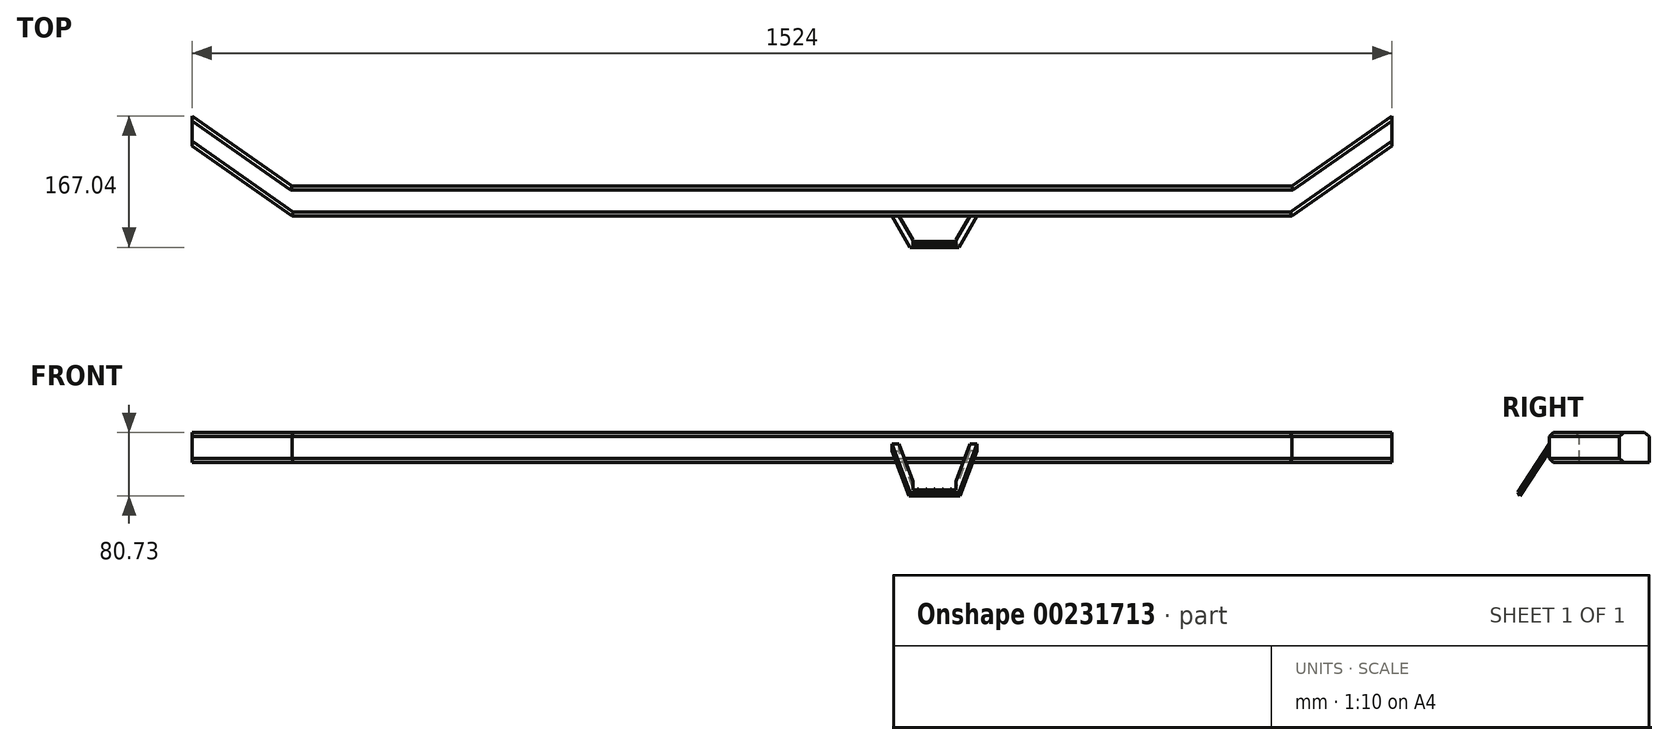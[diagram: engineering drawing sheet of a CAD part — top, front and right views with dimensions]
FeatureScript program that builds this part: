
annotation { "Feature Type Name" : "Feature", "Feature Type Description" : "" }
export const myFeature = defineFeature(function(context is Context, id is Id, definition is map)
    precondition{}
    {
        {
            var Q0;
            Q0=qCreatedBy(makeId("Top.planeOp"),FACE);
            var sketch = newSketch(context, id + "F0", { "sketchPlane" : qUnion([Q0])});
            skLineSegment(sketch, "E0", {"start": v(0, 0) * mm, "end": v(0, 180.16) * mm, "construction": true});
            skLineSegment(sketch, "E1", {"start": v(0, 0) * mm, "end": v(635, 0) * mm});
            skLineSegment(sketch, "E2", {"start": v(635, 0) * mm, "end": v(762, 88.9) * mm});
            skLineSegment(sketch, "E3.MirrorCS", {"start": v(0, 0) * mm, "end": v(-635, 0) * mm});
            skLineSegment(sketch, "E4.MirrorCS", {"start": v(-635, 0) * mm, "end": v(-762, 88.9) * mm});
            skSolve(sketch);
        }
        {
            var Q0;
            Q0=qCreatedBy(makeId("Right.planeOp"),FACE);
            var Q1;
            Q1=sQuery(id+"F0.wireOp",VERTEX,"E2.start");
            cPlane(context, id + "F1", {"entities" : qUnion([Q0, Q1]), "cplaneType" : CPlaneType.PLANE_POINT, "offset" : 25.4 * mm, "width" : 152.4 * mm, "height" : 152.4 * mm});
        }
        {
            var Q0;
            Q0=qCreatedBy(id+"F1.planeOp",FACE);
            var sketch = newSketch(context, id + "F2", { "sketchPlane" : qUnion([Q0])});
            skLineSegment(sketch, "E5.bottom", {"start": v(19.05, -19.05) * mm, "end": v(-19.05, -19.05) * mm});
            skLineSegment(sketch, "E5.top", {"start": v(19.05, 19.05) * mm, "end": v(-19.05, 19.05) * mm});
            skLineSegment(sketch, "E5.left", {"start": v(19.05, -19.05) * mm, "end": v(19.05, 19.05) * mm});
            skLineSegment(sketch, "E5.right", {"start": v(-19.05, -19.05) * mm, "end": v(-19.05, 19.05) * mm});
            skPoint(sketch, "E5.middle", {"position": v(0, 0) * mm});
            skSolve(sketch);
        }
        {
            var Q0;
            Q0=makeQuery(id+"F2.imprint","IMPRINT",FACE,{"disambiguationData":[TD([[makeQuery(id+"F2.imprint","IMPRINT",EDGE,{"derivedFrom":sQuery(id+"F2.wireOp",EDGE,"E5.bottom")}),-1.0]])]});
            var Q1;
            Q1=sQuery(id+"F0.wireOp",EDGE,"E2");
            sweep(context, id + "F3", {"profiles" : qUnion([Q0]), "path" : qUnion([Q1]), "keepProfileOrientation" : true});
        }
        {
            var Q0;
            Q0=makeQuery(id+"F2.imprint","IMPRINT",FACE,{"disambiguationData":[TD([[makeQuery(id+"F2.imprint","IMPRINT",EDGE,{"derivedFrom":sQuery(id+"F2.wireOp",EDGE,"E5.bottom")}),-1.0]])]});
            var Q1;
            Q1=sQuery(id+"F0.wireOp",EDGE,"E1");
            sweep(context, id + "F4", {"operationType" : NewBodyOperationType.ADD, "profiles" : qUnion([Q0]), "path" : qUnion([Q1])});
        }
        {
            var Q0;
            Q0=makeQuery(id+"F3.opSweep","SWEPT_BODY",BODY,{"disambiguationData":[OSD([sQuery(id+"F0.wireOp",EDGE,"E2"),sQuery(id+"F2.wireOp",EDGE,"E5.bottom"),sQuery(id+"F2.wireOp",EDGE,"E5.top"),sQuery(id+"F2.wireOp",EDGE,"E5.left"),sQuery(id+"F2.wireOp",EDGE,"E5.right")])]});
            var Q1;
            Q1=qCreatedBy(makeId("Right.planeOp"),FACE);
            mirror(context, id + "F5", {"operationType" : NewBodyOperationType.ADD, "entities" : qUnion([Q0]), "mirrorPlane" : qUnion([Q1])});
        }
        {
            var Q0;
            {var subQ0=makeQuery(id+"F4.opSweep","SWEPT_EDGE",EDGE,{"disambiguationData":[OSD([sQuery(id+"F0.wireOp",EDGE,"E1"),sQuery(id+"F2.wireOp",EDGE,"E5.top"),sQuery(id+"F2.wireOp",EDGE,"E5.right")])]});Q0=makeQuery(id+"F5.boolean.opBoolean","MERGE",EDGE,{"derivedFrom":[subQ0,makeQuery(id+"F5.opPattern","COPY",EDGE,{"derivedFrom":subQ0,"instanceName":"1"})]});}
            var Q1;
            Q1=makeQuery(id+"F5.opPattern","COPY",EDGE,{"derivedFrom":makeQuery(id+"F3.opSweep","SWEPT_EDGE",EDGE,{"disambiguationData":[OSD([sQuery(id+"F0.wireOp",EDGE,"E2"),sQuery(id+"F2.wireOp",EDGE,"E5.top"),sQuery(id+"F2.wireOp",EDGE,"E5.right")])]}),"instanceName":"1"});
            var Q2;
            Q2=makeQuery(id+"F5.opPattern","COPY",EDGE,{"derivedFrom":makeQuery(id+"F3.opSweep","SWEPT_EDGE",EDGE,{"disambiguationData":[OSD([sQuery(id+"F0.wireOp",EDGE,"E2"),sQuery(id+"F2.wireOp",EDGE,"E5.top"),sQuery(id+"F2.wireOp",EDGE,"E5.left")])]}),"instanceName":"1"});
            var Q3;
            {var subQ0=makeQuery(id+"F4.opSweep","SWEPT_EDGE",EDGE,{"disambiguationData":[OSD([sQuery(id+"F0.wireOp",EDGE,"E1"),sQuery(id+"F2.wireOp",EDGE,"E5.top"),sQuery(id+"F2.wireOp",EDGE,"E5.left")])]});Q3=makeQuery(id+"F5.boolean.opBoolean","MERGE",EDGE,{"derivedFrom":[subQ0,makeQuery(id+"F5.opPattern","COPY",EDGE,{"derivedFrom":subQ0,"instanceName":"1"})]});}
            var Q4;
            Q4=makeQuery(id+"F5.opPattern","COPY",EDGE,{"derivedFrom":makeQuery(id+"F3.opSweep","SWEPT_EDGE",EDGE,{"disambiguationData":[OSD([sQuery(id+"F0.wireOp",EDGE,"E2"),sQuery(id+"F2.wireOp",EDGE,"E5.bottom"),sQuery(id+"F2.wireOp",EDGE,"E5.right")])]}),"instanceName":"1"});
            var Q5;
            {var subQ0=makeQuery(id+"F4.opSweep","SWEPT_EDGE",EDGE,{"disambiguationData":[OSD([sQuery(id+"F0.wireOp",EDGE,"E1"),sQuery(id+"F2.wireOp",EDGE,"E5.bottom"),sQuery(id+"F2.wireOp",EDGE,"E5.right")])]});Q5=makeQuery(id+"F5.boolean.opBoolean","MERGE",EDGE,{"derivedFrom":[subQ0,makeQuery(id+"F5.opPattern","COPY",EDGE,{"derivedFrom":subQ0,"instanceName":"1"})]});}
            var Q6;
            Q6=makeQuery(id+"F3.opSweep","SWEPT_EDGE",EDGE,{"disambiguationData":[OSD([sQuery(id+"F0.wireOp",EDGE,"E2"),sQuery(id+"F2.wireOp",EDGE,"E5.top"),sQuery(id+"F2.wireOp",EDGE,"E5.right")])]});
            var Q7;
            Q7=makeQuery(id+"F3.opSweep","SWEPT_EDGE",EDGE,{"disambiguationData":[OSD([sQuery(id+"F0.wireOp",EDGE,"E2"),sQuery(id+"F2.wireOp",EDGE,"E5.top"),sQuery(id+"F2.wireOp",EDGE,"E5.left")])]});
            var Q8;
            Q8=makeQuery(id+"F3.opSweep","SWEPT_EDGE",EDGE,{"disambiguationData":[OSD([sQuery(id+"F0.wireOp",EDGE,"E2"),sQuery(id+"F2.wireOp",EDGE,"E5.bottom"),sQuery(id+"F2.wireOp",EDGE,"E5.right")])]});
            chamfer(context, id + "F6", {"entities" : qUnion([Q0, Q1, Q2, Q3, Q4, Q5, Q6, Q7, Q8]), "width" : 5.08 * mm, "tangentPropagation" : true});
        }
        {
            var Q0;
            Q0=makeQuery(id+"F3.opSweep","CAP_EDGE",EDGE,{"disambiguationData":[OSD([sQuery(id+"F0.wireOp",VERTEX,"E2.end"),sQuery(id+"F2.wireOp",EDGE,"E5.left")])],"isStart":false});
            cPlane(context, id + "F7", {"entities" : qUnion([Q0]), "cplaneType" : CPlaneType.LINE_ANGLE, "offset" : 25.4 * mm, "angle" : 30 * degree, "width" : 152.4 * mm, "height" : 152.4 * mm});
        }
        {
            var Q0;
            Q0=qCreatedBy(id+"F7.planeOp",FACE);
            cPlane(context, id + "F8", {"entities" : qUnion([Q0]), "cplaneType" : CPlaneType.OFFSET, "offset" : 609.6 * mm, "oppositeDirection" : true, "width" : 152.4 * mm, "height" : 152.4 * mm});
        }
        {
            var Q0;
            Q0=qCreatedBy(id+"F8.planeOp",FACE);
            var sketch = newSketch(context, id + "F9", { "sketchPlane" : qUnion([Q0])});
            skLineSegment(sketch, "E6", {"start": v(-82.2, 0) * mm, "end": v(-124.13, -55.87) * mm});
            skSolve(sketch);
        }
        {
            var Q0;
            {var subQ0=makeQuery(id+"F4.opSweep","SWEPT_FACE",FACE,{"disambiguationData":[OSD([sQuery(id+"F0.wireOp",EDGE,"E1"),sQuery(id+"F2.wireOp",EDGE,"E5.right")])]});Q0=makeQuery(id+"F5.boolean.opBoolean","MERGE",FACE,{"derivedFrom":[subQ0,makeQuery(id+"F5.opPattern","COPY",FACE,{"derivedFrom":subQ0,"instanceName":"1"})]});}
            var Q1;
            Q1=sQuery(id+"F9.wireOp",VERTEX,"E6.end");
            cPlane(context, id + "F10", {"entities" : qUnion([Q0, Q1]), "cplaneType" : CPlaneType.PLANE_POINT, "offset" : 25.4 * mm, "width" : 152.4 * mm, "height" : 152.4 * mm});
        }
        {
            var Q0;
            Q0=qCreatedBy(id+"F10.planeOp",FACE);
            var sketch = newSketch(context, id + "F11", { "sketchPlane" : qUnion([Q0])});
            skLineSegment(sketch, "E7", {"start": v(152.38, -55.87) * mm, "end": v(209.53, -55.87) * mm});
            skLineSegment(sketch, "E8", {"start": v(180.95, -55.87) * mm, "end": v(180.95, -95.2) * mm, "construction": true});
            skPoint(sketch, "E8.endSnap0", {"position": v(180.95, -55.87) * mm});
            skSolve(sketch);
        }
        {
            var Q0;
            Q0=makeQuery(id+"F3.opSweep","CAP_EDGE",EDGE,{"disambiguationData":[OSD([sQuery(id+"F0.wireOp",VERTEX,"E2.end"),sQuery(id+"F2.wireOp",EDGE,"E5.left")])],"isStart":false});
            cPlane(context, id + "F12", {"entities" : qUnion([Q0]), "cplaneType" : CPlaneType.LINE_ANGLE, "offset" : 25.4 * mm, "angle" : 330 * degree, "width" : 152.4 * mm, "height" : 152.4 * mm});
        }
        {
            var Q0;
            Q0=qCreatedBy(id+"F12.planeOp",FACE);
            var Q1;
            Q1=sQuery(id+"F11.wireOp",VERTEX,"E7.end");
            cPlane(context, id + "F13", {"entities" : qUnion([Q0, Q1]), "cplaneType" : CPlaneType.PLANE_POINT, "offset" : 25.4 * mm, "width" : 152.4 * mm, "height" : 152.4 * mm});
        }
        {
            var Q0;
            Q0=qCreatedBy(id+"F13.planeOp",FACE);
            var sketch = newSketch(context, id + "F14", { "sketchPlane" : qUnion([Q0])});
            skLineSegment(sketch, "E9", {"start": v(98.75, 0) * mm, "end": v(56.83, -55.87) * mm});
            skSolve(sketch);
        }
        {
            var Q0;
            {var subQ0=makeQuery(id+"F4.opSweep","SWEPT_FACE",FACE,{"disambiguationData":[OSD([sQuery(id+"F0.wireOp",EDGE,"E1"),sQuery(id+"F2.wireOp",EDGE,"E5.right")])]});Q0=makeQuery(id+"F5.boolean.opBoolean","MERGE",FACE,{"derivedFrom":[subQ0,makeQuery(id+"F5.opPattern","COPY",FACE,{"derivedFrom":subQ0,"instanceName":"1"})]});}
            var sketch = newSketch(context, id + "F15", { "sketchPlane" : qUnion([Q0])});
            skLineSegment(sketch, "E10.bottom", {"start": v(234.93, -4.44) * mm, "end": v(226.04, -4.44) * mm});
            skLineSegment(sketch, "E10.top", {"start": v(234.93, 4.45) * mm, "end": v(226.04, 4.44) * mm});
            skLineSegment(sketch, "E10.left", {"start": v(234.93, -4.44) * mm, "end": v(234.93, 4.45) * mm});
            skLineSegment(sketch, "E10.right", {"start": v(226.04, -4.44) * mm, "end": v(226.04, 4.44) * mm});
            skPoint(sketch, "E10.middle", {"position": v(230.49, 0) * mm});
            skSolve(sketch);
        }
        {
            var Q0;
            Q0=qCreatedBy(id+"F8.planeOp",FACE);
            var sketch = newSketch(context, id + "F16", { "sketchPlane" : qUnion([Q0])});
            skLineSegment(sketch, "E11", {"start": v(-82.2, 0) * mm, "end": v(-76.1, 8.13) * mm});
            skSolve(sketch);
        }
        {
            var Q0;
            Q0=makeQuery(id+"F15.imprint","IMPRINT",FACE,{"disambiguationData":[TD([[makeQuery(id+"F15.imprint","IMPRINT",EDGE,{"derivedFrom":sQuery(id+"F15.wireOp",EDGE,"E10.bottom")}),-1.0]])]});
            var Q1;
            Q1=sQuery(id+"F14.wireOp",EDGE,"E9");
            var Q2;
            Q2=sQuery(id+"F11.wireOp",EDGE,"E7");
            var Q3;
            Q3=sQuery(id+"F9.wireOp",EDGE,"E6");
            var Q4;
            Q4=sQuery(id+"F16.wireOp",EDGE,"E11");
            sweep(context, id + "F17", {"operationType" : NewBodyOperationType.ADD, "profiles" : qUnion([Q0]), "path" : qUnion([Q1, Q2, Q3, Q4])});
        }
        {
            var Q0;
            {var subQ0=makeQuery(id+"F4.opSweep","SWEPT_FACE",FACE,{"disambiguationData":[OSD([sQuery(id+"F0.wireOp",EDGE,"E1"),sQuery(id+"F2.wireOp",EDGE,"E5.right")])]});Q0=makeQuery(id+"F5.boolean.opBoolean","MERGE",FACE,{"derivedFrom":[subQ0,makeQuery(id+"F5.opPattern","COPY",FACE,{"derivedFrom":subQ0,"instanceName":"1"})]});}
            var Q1;
            Q1=makeQuery(id+"F17.opSweep","MID_CAP_VERTEX",VERTEX,{"disambiguationData":[OSD([sQuery(id+"F11.wireOp",EDGE,"E7"),sQuery(id+"F15.wireOp",EDGE,"E10.top"),sQuery(id+"F15.wireOp",EDGE,"E10.left")])],"capPos":2.0});
            cPlane(context, id + "F18", {"entities" : qUnion([Q0, Q1]), "cplaneType" : CPlaneType.PLANE_POINT, "offset" : 25.4 * mm, "width" : 152.4 * mm, "height" : 152.4 * mm});
        }
        {
            var Q0;
            Q0=qCreatedBy(id+"F18.planeOp",FACE);
            var sketch = newSketch(context, id + "F19", { "sketchPlane" : qUnion([Q0])});
            skLineSegment(sketch, "E12", {"start": v(180.95, -50.06) * mm, "end": v(180.95, -63.1) * mm, "construction": true});
            skLineSegment(sketch, "E13", {"start": v(153.65, -41.06) * mm, "end": v(180.95, -41.06) * mm});
            skLineSegment(sketch, "E14", {"start": v(153.65, -41.06) * mm, "end": v(153.65, -53.76) * mm});
            skLineSegment(sketch, "E15", {"start": v(153.65, -53.76) * mm, "end": v(180.95, -53.76) * mm});
            skLineSegment(sketch, "E16.MirrorCS", {"start": v(208.26, -53.76) * mm, "end": v(180.95, -53.76) * mm});
            skLineSegment(sketch, "E17.MirrorCS", {"start": v(208.26, -41.06) * mm, "end": v(208.26, -53.76) * mm});
            skLineSegment(sketch, "E18.MirrorCS", {"start": v(208.26, -41.06) * mm, "end": v(180.95, -41.06) * mm});
            skSolve(sketch);
        }
        {
            var Q0;
            Q0 = qSketchRegion(id + "F19", true);
            extrude(context, id + "F20", {"entities" : qUnion([Q0]), "operationType" : NewBodyOperationType.REMOVE, "oppositeDirection" : true, "depth" : 76.2 * mm});
        }
        {
            var Q0;
            Q0=makeQuery(id+"F20.boolean.opBoolean","COPY",FACE,{"derivedFrom":makeQuery(id+"F20.opExtrude","SWEPT_FACE",FACE,{"disambiguationData":[OSD([sQuery(id+"F19.wireOp",EDGE,"E15"),sQuery(id+"F19.wireOp",EDGE,"E16.MirrorCS")])]})});
            var sketch = newSketch(context, id + "F21", { "sketchPlane" : qUnion([Q0])});
            skCircle(sketch, "E19", {"center": v(160, -55.73) * mm, "radius": 0.76 * mm});
            skCircle(sketch, "E20.1.0.0", {"center": v(170.48, -55.73) * mm, "radius": 0.76 * mm});
            skCircle(sketch, "E20.2.0.0", {"center": v(180.95, -55.73) * mm, "radius": 0.76 * mm});
            skCircle(sketch, "E20.3.0.0", {"center": v(191.43, -55.73) * mm, "radius": 0.76 * mm});
            skCircle(sketch, "E20.4.0.0", {"center": v(201.9, -55.73) * mm, "radius": 0.76 * mm});
            skLineSegment(sketch, "E20.direction1", {"start": v(160, -55.73) * mm, "end": v(170.48, -55.73) * mm, "construction": true});
            skCircle(sketch, "E21.0.1.0", {"center": v(160, -53.29) * mm, "radius": 0.76 * mm});
            skLineSegment(sketch, "E21.direction1", {"start": v(160, -55.73) * mm, "end": v(185.4, -55.73) * mm, "construction": true});
            skLineSegment(sketch, "E21.direction2", {"start": v(160, -55.73) * mm, "end": v(160, -53.29) * mm, "construction": true});
            skCircle(sketch, "E22.1.0.0", {"center": v(170.48, -53.29) * mm, "radius": 0.76 * mm});
            skCircle(sketch, "E22.2.0.0", {"center": v(180.95, -53.29) * mm, "radius": 0.76 * mm});
            skCircle(sketch, "E22.3.0.0", {"center": v(191.43, -53.29) * mm, "radius": 0.76 * mm});
            skCircle(sketch, "E22.4.0.0", {"center": v(201.9, -53.29) * mm, "radius": 0.76 * mm});
            skLineSegment(sketch, "E22.direction1", {"start": v(160, -53.29) * mm, "end": v(170.48, -53.29) * mm, "construction": true});
            skSolve(sketch);
        }
        {
            var Q0;
            Q0 = qSketchRegion(id + "F21", true);
            extrude(context, id + "F22", {"entities" : qUnion([Q0]), "depth" : 0.76 * mm, "hasDraft" : true, "draftAngle" : 20 * degree, "draftPullDirection" : true});
        }
    });
